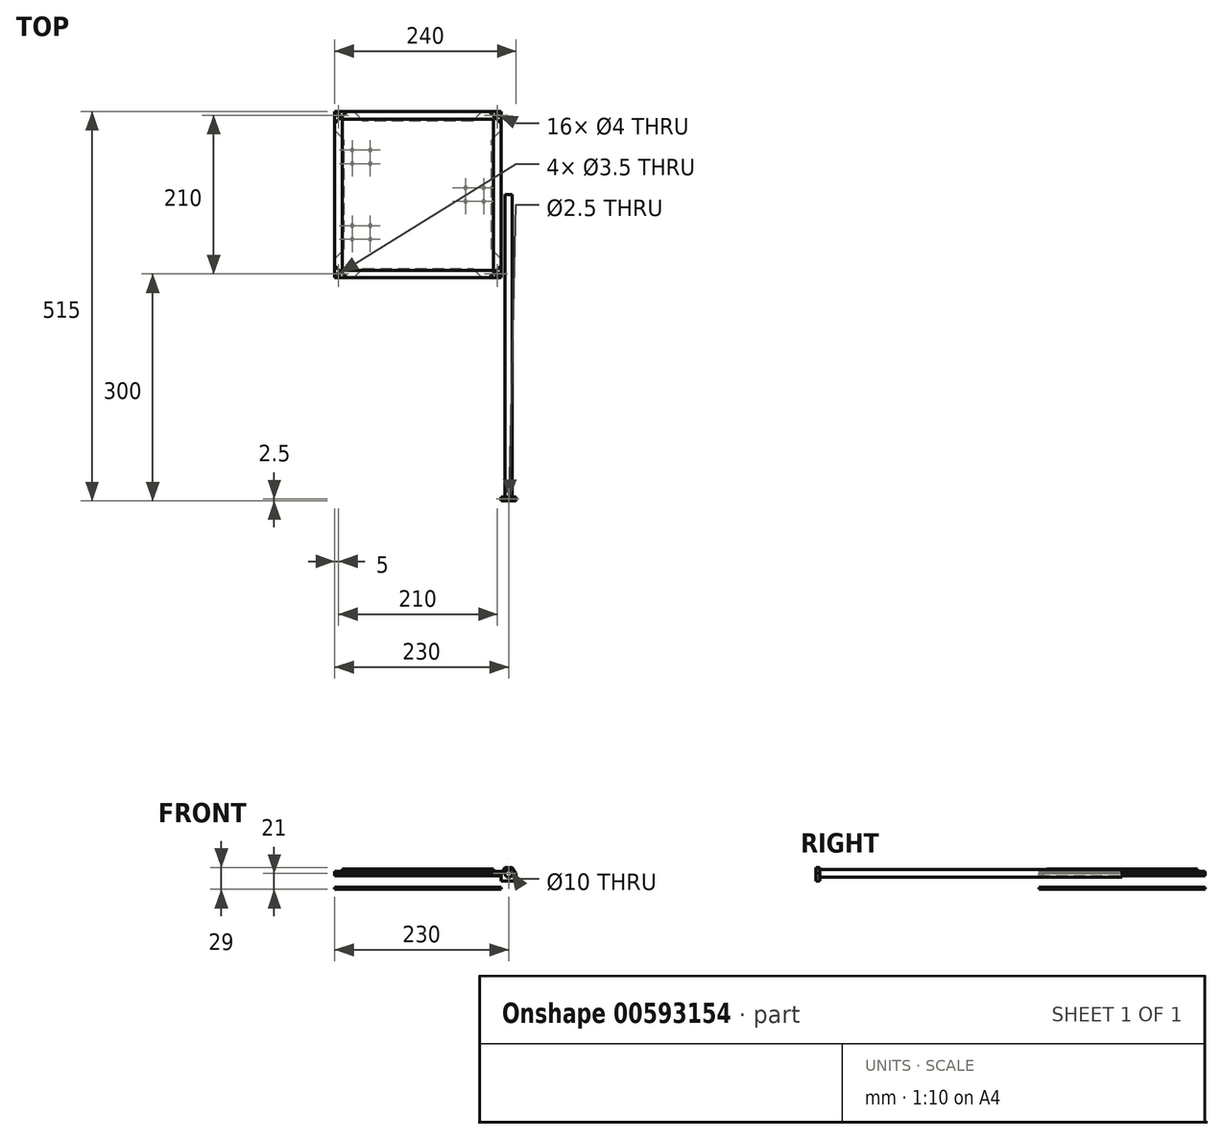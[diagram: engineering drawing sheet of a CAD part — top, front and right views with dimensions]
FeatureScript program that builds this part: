
annotation { "Feature Type Name" : "Feature", "Feature Type Description" : "" }
export const myFeature = defineFeature(function(context is Context, id is Id, definition is map)
    precondition{}
    {
        {
            var Q0;
            Q0=qCreatedBy(makeId("Top.planeOp"),FACE);
            var sketch = newSketch(context, id + "F0", { "sketchPlane" : qUnion([Q0])});
            skLineSegment(sketch, "E0", {"start": v(110, 0) * mm, "end": v(110, 94) * mm});
            skLineSegment(sketch, "E1", {"start": v(110, 94) * mm, "end": v(94, 110) * mm});
            skLineSegment(sketch, "E2", {"start": v(94, 110) * mm, "end": v(0, 110) * mm});
            skLineSegment(sketch, "E3.MirrorCS", {"start": v(-94, 110) * mm, "end": v(0, 110) * mm});
            skLineSegment(sketch, "E4.MirrorCS", {"start": v(-110, 94) * mm, "end": v(-94, 110) * mm});
            skLineSegment(sketch, "E5.MirrorCS", {"start": v(-110, 0) * mm, "end": v(-110, 94) * mm});
            skLineSegment(sketch, "E6.MirrorCS", {"start": v(-110, 0) * mm, "end": v(-110, -94) * mm});
            skLineSegment(sketch, "E7.MirrorCS", {"start": v(-110, -94) * mm, "end": v(-94, -110) * mm});
            skLineSegment(sketch, "E8.MirrorCS", {"start": v(-94, -110) * mm, "end": v(0, -110) * mm});
            skLineSegment(sketch, "E9.MirrorCS", {"start": v(94, -110) * mm, "end": v(0, -110) * mm});
            skLineSegment(sketch, "E10.MirrorCS", {"start": v(110, -94) * mm, "end": v(94, -110) * mm});
            skLineSegment(sketch, "E11.MirrorCS", {"start": v(110, 0) * mm, "end": v(110, -94) * mm});
            skSolve(sketch);
        }
        {
            var Q0;
            Q0=makeQuery(id+"F0.imprint","IMPRINT",FACE,{"disambiguationData":[TD([[makeQuery(id+"F0.imprint","IMPRINT",EDGE,{"derivedFrom":sQuery(id+"F0.wireOp",EDGE,"E0")}),1.0]])]});
            extrude(context, id + "F1", {"entities" : qUnion([Q0]), "depth" : 3 * mm, "offsetDistance" : 25 * mm});
        }
        {
            var Q0;
            Q0=makeQuery(id+"F1.opExtrude","CAP_FACE",FACE,{"disambiguationData":[OSD([sQuery(id+"F0.wireOp",EDGE,"E0"),sQuery(id+"F0.wireOp",EDGE,"E1"),sQuery(id+"F0.wireOp",EDGE,"E2"),sQuery(id+"F0.wireOp",EDGE,"E3.MirrorCS"),sQuery(id+"F0.wireOp",EDGE,"E4.MirrorCS"),sQuery(id+"F0.wireOp",EDGE,"E5.MirrorCS"),sQuery(id+"F0.wireOp",EDGE,"E6.MirrorCS"),sQuery(id+"F0.wireOp",EDGE,"E7.MirrorCS"),sQuery(id+"F0.wireOp",EDGE,"E8.MirrorCS"),sQuery(id+"F0.wireOp",EDGE,"E9.MirrorCS"),sQuery(id+"F0.wireOp",EDGE,"E10.MirrorCS"),sQuery(id+"F0.wireOp",EDGE,"E11.MirrorCS")])],"isStart":false});
            var sketch = newSketch(context, id + "F2", { "sketchPlane" : qUnion([Q0])});
            skLineSegment(sketch, "E12.bottom", {"start": v(100, -100) * mm, "end": v(-100, -100) * mm});
            skLineSegment(sketch, "E12.top", {"start": v(100, 100) * mm, "end": v(-100, 100) * mm});
            skLineSegment(sketch, "E12.left", {"start": v(100, -100) * mm, "end": v(100, 100) * mm});
            skLineSegment(sketch, "E12.right", {"start": v(-100, -100) * mm, "end": v(-100, 100) * mm});
            skPoint(sketch, "E12.middle", {"position": v(0, 0) * mm});
            skSolve(sketch);
        }
        {
            var Q0;
            Q0=makeQuery(id+"F2.imprint","IMPRINT",FACE,{"disambiguationData":[TD([[makeQuery(id+"F2.imprint","IMPRINT",EDGE,{"derivedFrom":sQuery(id+"F2.wireOp",EDGE,"E12.bottom")}),-1.0]])]});
            extrude(context, id + "F3", {"entities" : qUnion([Q0]), "depth" : 3 * mm, "offsetDistance" : 25 * mm});
        }
        {
            var Q0;
            Q0=makeQuery(id+"F0.imprint","IMPRINT",FACE,{"disambiguationData":[TD([[makeQuery(id+"F0.imprint","IMPRINT",EDGE,{"derivedFrom":sQuery(id+"F0.wireOp",EDGE,"E0")}),1.0]])]});
            var sketch = newSketch(context, id + "F4", { "sketchPlane" : qUnion([Q0])});
            skLineSegment(sketch, "E13.bottom", {"start": v(110, -110) * mm, "end": v(-110, -110) * mm});
            skLineSegment(sketch, "E13.top", {"start": v(110, 110) * mm, "end": v(-110, 110) * mm});
            skLineSegment(sketch, "E13.left", {"start": v(110, -110) * mm, "end": v(110, 110) * mm});
            skLineSegment(sketch, "E13.right", {"start": v(-110, -110) * mm, "end": v(-110, 110) * mm});
            skPoint(sketch, "E13.middle", {"position": v(0, 0) * mm});
            skCircle(sketch, "E14", {"center": v(105, -105) * mm, "radius": 1.75 * mm});
            skCircle(sketch, "E15.MirrorC", {"center": v(-105, -105) * mm, "radius": 1.75 * mm});
            skCircle(sketch, "E16.MirrorC", {"center": v(105, 105) * mm, "radius": 1.75 * mm});
            skCircle(sketch, "E17.MirrorC", {"center": v(-105, 105) * mm, "radius": 1.75 * mm});
            skSolve(sketch);
        }
        {
            var Q0;
            Q0 = qSketchRegion(id + "F4", true);
            extrude(context, id + "F5", {"entities" : qUnion([Q0]), "depth" : -3 * mm, "offsetDistance" : 25 * mm});
        }
        {
            var Q0;
            Q0=makeQuery(id+"F5.opExtrude","CAP_FACE",FACE,{"disambiguationData":[OSD([sQuery(id+"F4.wireOp",EDGE,"E13.bottom"),sQuery(id+"F4.wireOp",EDGE,"E13.top"),sQuery(id+"F4.wireOp",EDGE,"E13.left"),sQuery(id+"F4.wireOp",EDGE,"E13.right"),sQuery(id+"F4.wireOp",EDGE,"E14"),sQuery(id+"F4.wireOp",EDGE,"E15.MirrorC"),sQuery(id+"F4.wireOp",EDGE,"E16.MirrorC"),sQuery(id+"F4.wireOp",EDGE,"E17.MirrorC")])],"isStart":false});
            cPlane(context, id + "F6", {"entities" : qUnion([Q0]), "cplaneType" : CPlaneType.OFFSET, "offset" : 15 * mm, "width" : 150 * mm, "height" : 150 * mm});
        }
        {
            var Q0;
            Q0=qCreatedBy(id+"F6.planeOp",FACE);
            var sketch = newSketch(context, id + "F7", { "sketchPlane" : qUnion([Q0])});
            skLineSegment(sketch, "E18", {"start": v(0, 97.5) * mm, "end": v(72.5, 97.5) * mm});
            skLineSegment(sketch, "E19", {"start": v(72.5, 97.5) * mm, "end": v(85, 110) * mm});
            skLineSegment(sketch, "E20", {"start": v(85, 110) * mm, "end": v(110, 110) * mm});
            skLineSegment(sketch, "E21", {"start": v(110, 110) * mm, "end": v(110, 85) * mm});
            skLineSegment(sketch, "E22", {"start": v(110, 85) * mm, "end": v(97.5, 72.5) * mm});
            skLineSegment(sketch, "E23", {"start": v(97.5, 72.5) * mm, "end": v(97.5, -3.4) * mm});
            skLineSegment(sketch, "E24.MirrorCS", {"start": v(0, -97.5) * mm, "end": v(72.5, -97.5) * mm});
            skLineSegment(sketch, "E25.MirrorCS", {"start": v(72.5, -97.5) * mm, "end": v(85, -110) * mm});
            skLineSegment(sketch, "E26.MirrorCS", {"start": v(85, -110) * mm, "end": v(110, -110) * mm});
            skLineSegment(sketch, "E27.MirrorCS", {"start": v(110, -110) * mm, "end": v(110, -85) * mm});
            skLineSegment(sketch, "E28.MirrorCS", {"start": v(110, -85) * mm, "end": v(97.5, -72.5) * mm});
            skLineSegment(sketch, "E29.MirrorCS", {"start": v(97.5, -72.5) * mm, "end": v(97.5, 3.4) * mm});
            skLineSegment(sketch, "E30.MirrorCS", {"start": v(0, 97.5) * mm, "end": v(-72.5, 97.5) * mm});
            skLineSegment(sketch, "E31.MirrorCS", {"start": v(-72.5, 97.5) * mm, "end": v(-85, 110) * mm});
            skLineSegment(sketch, "E32.MirrorCS", {"start": v(-85, 110) * mm, "end": v(-110, 110) * mm});
            skLineSegment(sketch, "E33.MirrorCS", {"start": v(-110, 110) * mm, "end": v(-110, 85) * mm});
            skLineSegment(sketch, "E34.MirrorCS", {"start": v(-110, 85) * mm, "end": v(-97.5, 72.5) * mm});
            skLineSegment(sketch, "E35.MirrorCS", {"start": v(-97.5, 72.5) * mm, "end": v(-97.5, -3.4) * mm});
            skLineSegment(sketch, "E36.MirrorCS", {"start": v(-97.5, -72.5) * mm, "end": v(-97.5, 3.4) * mm});
            skLineSegment(sketch, "E37.MirrorCS", {"start": v(-110, -85) * mm, "end": v(-97.5, -72.5) * mm});
            skLineSegment(sketch, "E38.MirrorCS", {"start": v(-110, -110) * mm, "end": v(-110, -85) * mm});
            skLineSegment(sketch, "E39.MirrorCS", {"start": v(-85, -110) * mm, "end": v(-110, -110) * mm});
            skLineSegment(sketch, "E40.MirrorCS", {"start": v(-72.5, -97.5) * mm, "end": v(-85, -110) * mm});
            skLineSegment(sketch, "E41.MirrorCS", {"start": v(0, -97.5) * mm, "end": v(-72.5, -97.5) * mm});
            skCircle(sketch, "E42", {"center": v(-105, 105) * mm, "radius": 2 * mm});
            skCircle(sketch, "E43.MirrorC", {"center": v(105, 105) * mm, "radius": 2 * mm});
            skCircle(sketch, "E44.MirrorC", {"center": v(-105, -105) * mm, "radius": 2 * mm});
            skCircle(sketch, "E45.MirrorC", {"center": v(105, -105) * mm, "radius": 2 * mm});
            skLineSegment(sketch, "E46", {"start": v(75, 84.91) * mm, "end": v(75, -61.74) * mm, "construction": true});
            skLineSegment(sketch, "E47", {"start": v(-75, 86.28) * mm, "end": v(-75, -56.84) * mm, "construction": true});
            skLineSegment(sketch, "E48", {"start": v(-93.08, 0) * mm, "end": v(91.43, 0) * mm, "construction": true});
            skCircle(sketch, "E49", {"center": v(63, 9) * mm, "radius": 2 * mm});
            skCircle(sketch, "E50.MirrorC", {"center": v(87, 9) * mm, "radius": 2 * mm});
            skCircle(sketch, "E51.MirrorC", {"center": v(63, -9) * mm, "radius": 2 * mm});
            skCircle(sketch, "E52.MirrorC", {"center": v(87, -9) * mm, "radius": 2 * mm});
            skLineSegment(sketch, "E53", {"start": v(-89.93, -50) * mm, "end": v(89.8, -50) * mm, "construction": true});
            skLineSegment(sketch, "E54", {"start": v(-88.55, 50) * mm, "end": v(89.8, 50) * mm, "construction": true});
            skCircle(sketch, "E55", {"center": v(-63, -41) * mm, "radius": 2 * mm});
            skCircle(sketch, "E56.MirrorC", {"center": v(-63, -59) * mm, "radius": 2 * mm});
            skCircle(sketch, "E57.MirrorC", {"center": v(-87, -59) * mm, "radius": 2 * mm});
            skCircle(sketch, "E58.MirrorC", {"center": v(-87, -41) * mm, "radius": 2 * mm});
            skCircle(sketch, "E59.MirrorC", {"center": v(-87, 41) * mm, "radius": 2 * mm});
            skCircle(sketch, "E60.MirrorC", {"center": v(-63, 41) * mm, "radius": 2 * mm});
            skCircle(sketch, "E61.MirrorC", {"center": v(-63, 59) * mm, "radius": 2 * mm});
            skCircle(sketch, "E62.MirrorC", {"center": v(-87, 59) * mm, "radius": 2 * mm});
            skSolve(sketch);
        }
        {
            var Q0;
            Q0 = qSketchRegion(id + "F7", true);
            extrude(context, id + "F8", {"entities" : qUnion([Q0]), "depth" : 3 * mm, "offsetDistance" : 25 * mm});
        }
        {
            var Q0;
            Q0=qCreatedBy(makeId("Front.planeOp"),FACE);
            var sketch = newSketch(context, id + "F9", { "sketchPlane" : qUnion([Q0])});
            skCircle(sketch, "E63", {"center": v(120, 0) * mm, "radius": 5 * mm});
            skSolve(sketch);
        }
        {
            var Q0;
            Q0=makeQuery(id+"F9.imprint","IMPRINT",FACE,{"disambiguationData":[TD([[makeQuery(id+"F9.imprint","IMPRINT",EDGE,{"derivedFrom":sQuery(id+"F9.wireOp",EDGE,"E63")}),1.0]])]});
            extrude(context, id + "F10", {"entities" : qUnion([Q0]), "depth" : 400 * mm, "offsetDistance" : 25 * mm});
        }
        {
            var Q0;
            Q0=makeQuery(id+"F10.opExtrude","CAP_FACE",FACE,{"disambiguationData":[OSD([sQuery(id+"F9.wireOp",EDGE,"E63")])],"isStart":false});
            var sketch = newSketch(context, id + "F11", { "sketchPlane" : qUnion([Q0])});
            skLineSegment(sketch, "E64", {"start": v(110, -10) * mm, "end": v(130, -10) * mm});
            skLineSegment(sketch, "E65", {"start": v(130, -10) * mm, "end": v(130, 0) * mm});
            skLineSegment(sketch, "E66", {"start": v(130, 0) * mm, "end": v(125, 8) * mm});
            skLineSegment(sketch, "E67", {"start": v(125, 8) * mm, "end": v(115, 8) * mm});
            skLineSegment(sketch, "E68", {"start": v(115, 8) * mm, "end": v(110, 0) * mm});
            skLineSegment(sketch, "E69", {"start": v(110, 0) * mm, "end": v(110, -10) * mm});
            skCircle(sketch, "E70", {"center": v(120, 0) * mm, "radius": 5 * mm});
            skSolve(sketch);
        }
        {
            var Q0;
            Q0 = qSketchRegion(id + "F11", true);
            extrude(context, id + "F12", {"entities" : qUnion([Q0]), "depth" : 5 * mm, "offsetDistance" : 25 * mm});
        }
        {
            var Q0;
            Q0=makeQuery(id+"F12.opExtrude","SWEPT_FACE",FACE,{"disambiguationData":[OSD([sQuery(id+"F11.wireOp",EDGE,"E67")])]});
            var sketch = newSketch(context, id + "F13", { "sketchPlane" : qUnion([Q0])});
            skCircle(sketch, "E71", {"center": v(120, -402.5) * mm, "radius": 1.6 * mm});
            skSolve(sketch);
        }
        {
            var Q0;
            Q0=sQuery(id+"F13.wireOp",VERTEX,"E71.center");
            var Q1;
            Q1=makeQuery(id+"F12.opExtrude","SWEPT_BODY",BODY,{"disambiguationData":[OSD([sQuery(id+"F11.wireOp",EDGE,"E64"),sQuery(id+"F11.wireOp",EDGE,"E65"),sQuery(id+"F11.wireOp",EDGE,"E66"),sQuery(id+"F11.wireOp",EDGE,"E67"),sQuery(id+"F11.wireOp",EDGE,"E68"),sQuery(id+"F11.wireOp",EDGE,"E69"),sQuery(id+"F11.wireOp",EDGE,"E70")])]});
            hole(context, id + "F14", {"style" : HoleStyle.SIMPLE, "endStyle" : HoleEndStyle.BLIND, "standardTappedOrClearance" : lookupTablePath({ "standard" : "ISO", "engagement" : "75%", "pitch" : "0.5 mm", "size" : "M3", "type" : "Tapped" }), "standardBlindInLast" : lookupTablePath({ "standard" : "ISO", "engagement" : "75%", "pitch" : "0.5 mm", "size" : "M3", "type" : "Tapped" }), "holeDiameter" : 2.5 * mm, "majorDiameter" : 3 * mm, "showTappedDepth" : true, "holeDepth" : 5 * mm, "isTappedThrough" : true, "tappedDepth" : 3.5 * mm, "tapClearance" : 3, "locations" : qUnion([Q0]), "scope" : qUnion([Q1])});
        }
    });
